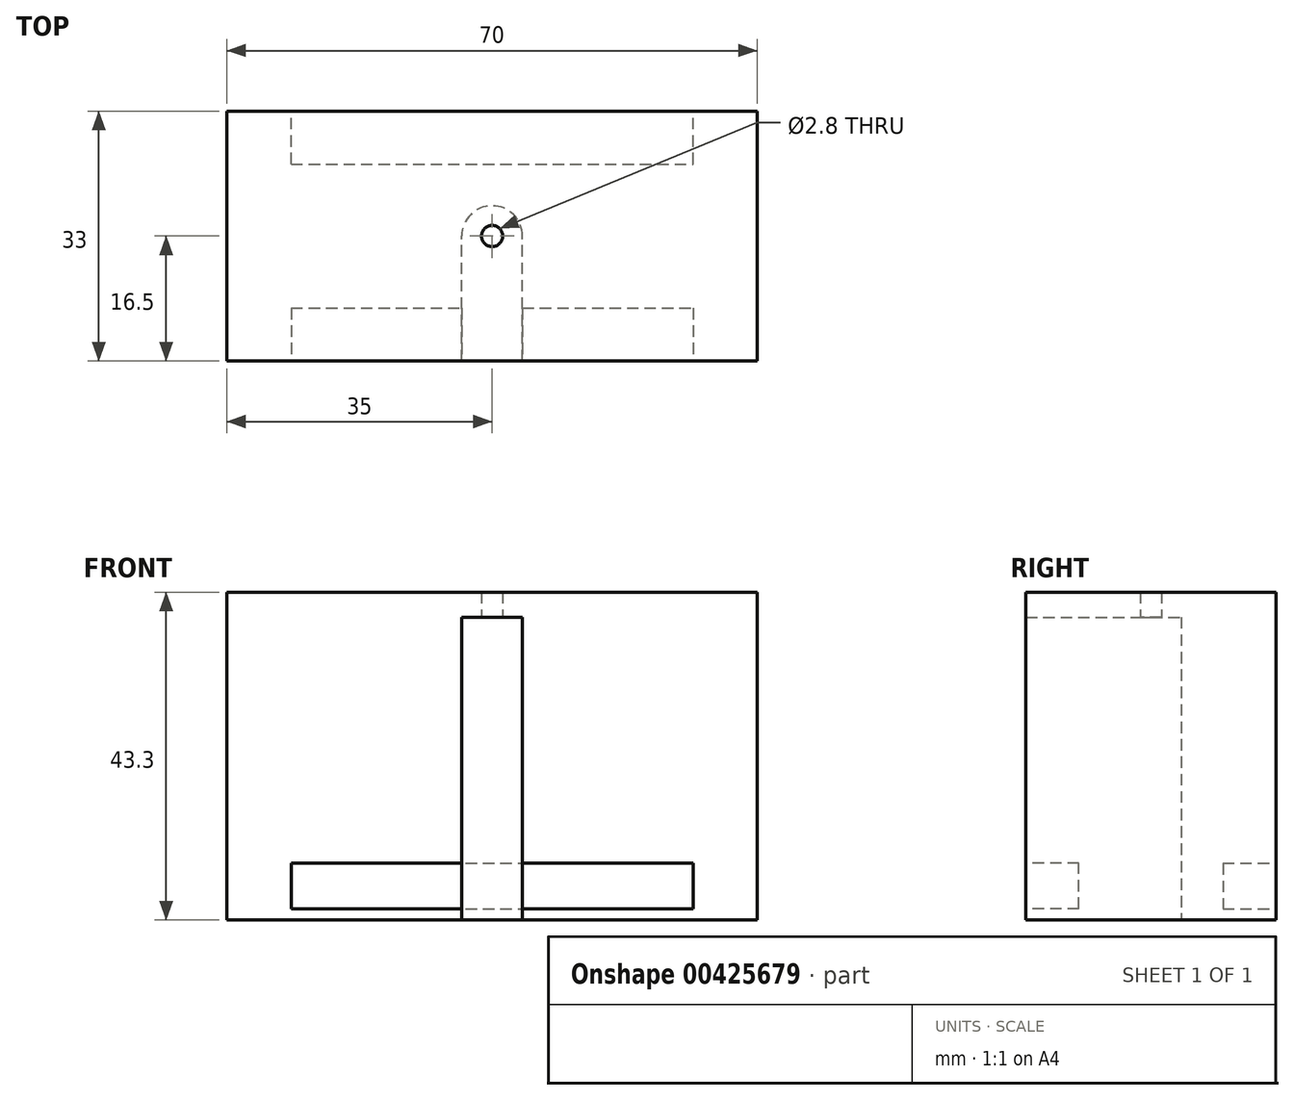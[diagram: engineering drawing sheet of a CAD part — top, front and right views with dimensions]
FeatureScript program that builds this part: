
annotation { "Feature Type Name" : "Feature", "Feature Type Description" : "" }
export const myFeature = defineFeature(function(context is Context, id is Id, definition is map)
    precondition{}
    {
        {
            var Q0;
            Q0=qCreatedBy(makeId("Top.planeOp"),FACE);
            var sketch = newSketch(context, id + "F0", { "sketchPlane" : qUnion([Q0])});
            skLineSegment(sketch, "E0.bottom", {"start": v(-35, 16.5) * mm, "end": v(35, 16.5) * mm});
            skLineSegment(sketch, "E0.top", {"start": v(-35, -16.5) * mm, "end": v(35, -16.5) * mm});
            skLineSegment(sketch, "E0.left", {"start": v(-35, 16.5) * mm, "end": v(-35, -16.5) * mm});
            skLineSegment(sketch, "E0.right", {"start": v(35, 16.5) * mm, "end": v(35, -16.5) * mm});
            skCircle(sketch, "E1", {"center": v(0, 0) * mm, "radius": 1.4 * mm});
            skSolve(sketch);
        }
        {
            var Q0;
            Q0 = qSketchRegion(id + "F0", true);
            extrude(context, id + "F1", {"entities" : qUnion([Q0]), "depth" : 43.3 * mm, "offsetDistance" : 25 * mm});
        }
        {
            var Q0;
            Q0=makeQuery(id+"F1.opExtrude","CAP_FACE",FACE,{"disambiguationData":[OSD([sQuery(id+"F0.wireOp",EDGE,"E0.bottom"),sQuery(id+"F0.wireOp",EDGE,"E0.top"),sQuery(id+"F0.wireOp",EDGE,"E0.left"),sQuery(id+"F0.wireOp",EDGE,"E0.right")])],"isStart":true});
            var sketch = newSketch(context, id + "F2", { "sketchPlane" : qUnion([Q0])});
            skLineSegment(sketch, "E2.bottom", {"start": v(-4, 18.44) * mm, "end": v(4, 18.44) * mm});
            skLineSegment(sketch, "E2.left", {"start": v(-4, 18.44) * mm, "end": v(-4, 0) * mm});
            skLineSegment(sketch, "E2.right", {"start": v(4, 18.44) * mm, "end": v(4, 0) * mm});
            skArc(sketch, "E3", {"start": v(-4, 0) * mm, "mid": v(0, -4) * mm, "end": v(4, 0) * mm});
            skSolve(sketch);
        }
        {
            var Q0;
            Q0 = qSketchRegion(id + "F2", true);
            extrude(context, id + "F3", {"entities" : qUnion([Q0]), "operationType" : NewBodyOperationType.REMOVE, "oppositeDirection" : true, "depth" : 40 * mm, "offsetDistance" : 25 * mm});
        }
        {
            var Q0;
            Q0=makeQuery(id+"F1.opExtrude","SWEPT_FACE",FACE,{"disambiguationData":[OSD([sQuery(id+"F0.wireOp",EDGE,"E0.top")])]});
            var sketch = newSketch(context, id + "F4", { "sketchPlane" : qUnion([Q0])});
            skLineSegment(sketch, "E4.bottom", {"start": v(-26.5, 7.5) * mm, "end": v(26.5, 7.5) * mm});
            skLineSegment(sketch, "E4.top", {"start": v(-26.5, 1.5) * mm, "end": v(26.5, 1.5) * mm});
            skLineSegment(sketch, "E4.left", {"start": v(-26.5, 7.5) * mm, "end": v(-26.5, 1.5) * mm});
            skLineSegment(sketch, "E4.right", {"start": v(26.5, 7.5) * mm, "end": v(26.5, 1.5) * mm});
            skSolve(sketch);
        }
        {
            var Q0;
            Q0 = qSketchRegion(id + "F4", true);
            extrude(context, id + "F5", {"entities" : qUnion([Q0]), "operationType" : NewBodyOperationType.REMOVE, "oppositeDirection" : true, "depth" : 7 * mm, "offsetDistance" : 25 * mm});
        }
        {
            var Q0;
            Q0=makeQuery(id+"F1.opExtrude","SWEPT_FACE",FACE,{"disambiguationData":[OSD([sQuery(id+"F0.wireOp",EDGE,"E0.bottom")])]});
            var sketch = newSketch(context, id + "F6", { "sketchPlane" : qUnion([Q0])});
            skLineSegment(sketch, "E5.0", {"start": v(-26.5, 7.5) * mm, "end": v(-26.5, 1.5) * mm});
            skLineSegment(sketch, "E6.0", {"start": v(26.5, 7.5) * mm, "end": v(-26.5, 7.5) * mm});
            skLineSegment(sketch, "E7.0", {"start": v(26.5, 7.5) * mm, "end": v(26.5, 1.5) * mm});
            skLineSegment(sketch, "E8.0", {"start": v(26.5, 1.5) * mm, "end": v(-26.5, 1.5) * mm});
            skSolve(sketch);
        }
        {
            var Q0;
            Q0 = qSketchRegion(id + "F6", true);
            extrude(context, id + "F7", {"entities" : qUnion([Q0]), "operationType" : NewBodyOperationType.REMOVE, "oppositeDirection" : true, "depth" : 7 * mm, "offsetDistance" : 25 * mm});
        }
    });
